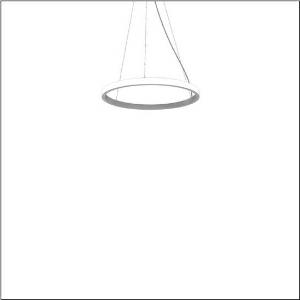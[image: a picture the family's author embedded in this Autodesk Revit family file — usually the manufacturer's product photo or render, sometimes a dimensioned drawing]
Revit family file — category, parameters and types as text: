
# Revit family: silica_r__21_ring-o_5pjbo1d1204a_83b6
name_source: partatom
category: Lighting Fixtures
units: mm (PartAtom-declared; Revit-internal decimal feet)

## family parameters
Cut with Voids When Loaded = No
Host = Face
Light Source = No
Part Type = Normal
Room Calculation Point = No
Round Connector Dimension = Use Diameter
Shared = No

## types (1)
- Silica® 21 Ring-O (1 x LED, 3740 lm, 60 W, 3000K)
    Apparent Load = 60 VA
    CIE Flux Codes = 2 16 49 50 100
    Color Rendering = 80
    Color Temperature = 3000K
    Default Elevation = 1800 mm
    Description = Silica® 21 Ring-O, suspended luminaire, of PMMA, frosted, light emission: outer ring side luminous distribution, primary light characteristic: symmetric, installation type: suspended mounting, LED, rated luminous flux: 3.744lm, luminous efficacy: 62lm/W, light colour: 830, colour temperature: 3000K, control gear: DALI 2, with terminal, 5-pole, mains connection: 230V, AC/DC, 0/50..60Hz, rated input power: 60W, housing, of extruded aluminium section, metallic grey (RAL 9006), diameter: 610mm, ceiling canopy, metallic grey (RAL 9006), protection rating (lamp compartment): IP40, insulation class (complete): insulation class I (protective earthing), certification: CE, impact resistance: IK02, permissible operating ambient temperature: 0..+35°C, packaging unit: 1 piece
    Height = 48 mm
    Lamp = 1 x LED
    Lamp Light Flux = 3740 lm
    Lamp Power = 60 W
    Lamp count = 1
    Length = 610 mm
    Luminous efficacy = 62 lm/W
    Manufacturer = Siteco
    ModVariant = No
    Model = 5PJBO1D1204A
    Mounting Place = Ceiling
    Mounting Type = Pendant
    Number of Poles = 1
    OnlyDefault = Yes
    Power Factor = 1
    Product Name = Silica® 21 Ring-O
    Product group = suspended luminaire
    ProductGroupID = 905
    Protection Class = Protection class I
    Protection Degree = IP 40
    RLX_Detail_Level = 1
    RLX_Emergency_Light_Flux = 0 lm
    RLX_Emergency_Type = 0
    RLX_Emergency_Type_DB = No
    RlxData = <blob elided: 11629 chars, md5=b9cd9c06>
    Socket = socket
    Standby Power = 0 W
    System Light Flux = 3740 lm
    System Power = 60 W
    Type Comments = Product without accessories
    Type Image = l_1251758.jpg
    URL = http://relux.com
    VarID = ---
    Voltage = 0 V
    Weight = 0.00 kg
    Width = 0 mm  [stored 0 ft]

note: [stored X ft] marks values corroborated as IEEE doubles in the binary element streams (Revit-internal decimal feet)

## geometry (parser evidence)
native form markers: Sweep x11
no freeform markers — native parametric forms only
